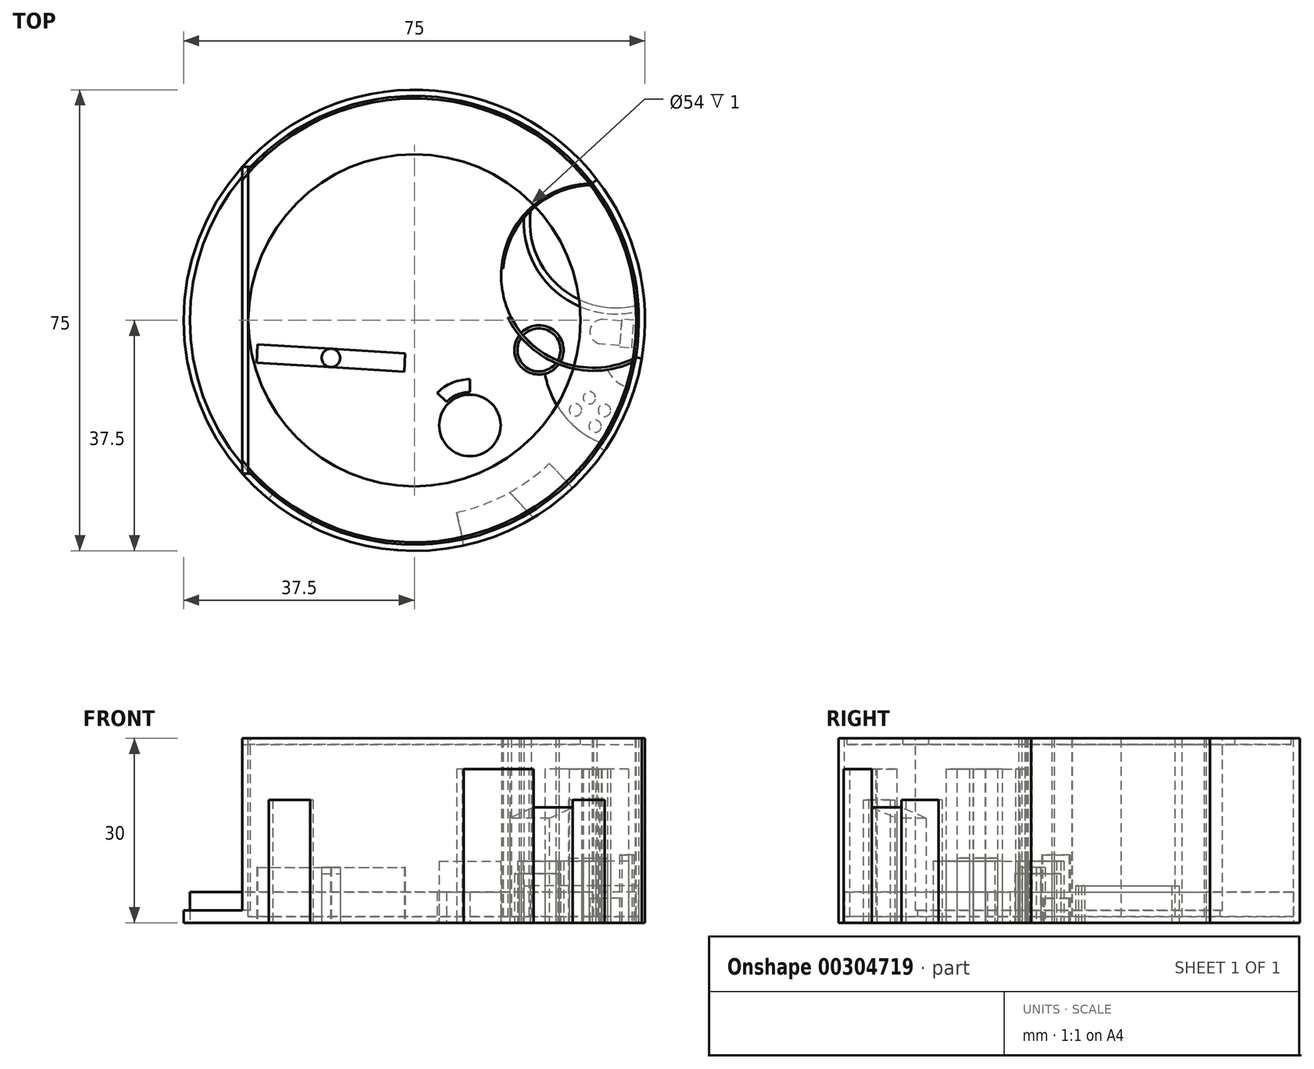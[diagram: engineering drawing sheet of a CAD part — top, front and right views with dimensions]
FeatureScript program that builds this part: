
annotation { "Feature Type Name" : "Feature", "Feature Type Description" : "" }
export const myFeature = defineFeature(function(context is Context, id is Id, definition is map)
    precondition{}
    {
        {
            var Q0;
            Q0=qCreatedBy(makeId("Top.planeOp"),FACE);
            var sketch = newSketch(context, id + "F0", { "sketchPlane" : qUnion([Q0])});
            skCircle(sketch, "E0", {"center": v(0, 0) * mm, "radius": 37.5 * mm});
            skSolve(sketch);
        }
        {
            var Q0;
            Q0=makeQuery(id+"F0.imprint","IMPRINT",FACE,{"disambiguationData":[TD([[makeQuery(id+"F0.imprint","IMPRINT",EDGE,{"derivedFrom":sQuery(id+"F0.wireOp",EDGE,"E0")}),1.0]])]});
            extrude(context, id + "F1", {"entities" : qUnion([Q0]), "oppositeDirection" : true, "depth" : 30 * mm});
        }
        {
            var Q0;
            Q0=qSketchRegion(id+"F0",true);
            var sketch = newSketch(context, id + "F2", { "sketchPlane" : qUnion([Q0])});
            skLineSegment(sketch, "E1", {"start": v(-28, 24.94) * mm, "end": v(-28, -24.94) * mm});
            skSolve(sketch);
        }
        {
            var Q0;
            {var subQ0=sQuery(id+"F2.wireOp",EDGE,"E1");Q0=makeQuery(id+"F2.imprint","IMPRINT",FACE,{"disambiguationData":[TD([[makeQuery(id+"F2.imprint","IMPRINT",EDGE,{"derivedFrom":subQ0}),-1.0]])]});}
            extrude(context, id + "F3", {"entities" : qUnion([Q0]), "operationType" : NewBodyOperationType.REMOVE, "oppositeDirection" : true, "depth" : 28 * mm});
        }
        {
            var Q0;
            {var subQ0=sQuery(id+"F2.wireOp",EDGE,"E1");Q0=makeQuery(id+"F2.imprint","IMPRINT",FACE,{"disambiguationData":[TD([[makeQuery(id+"F2.imprint","IMPRINT",EDGE,{"derivedFrom":subQ0}),1.0]])]});}
            var sketch = newSketch(context, id + "F4", { "sketchPlane" : qUnion([Q0])});
            skCircle(sketch, "E2", {"center": v(0, 0) * mm, "radius": 27 * mm});
            skArc(sketch, "E3", {"start": v(-28, 22.79) * mm, "mid": v(36.1, 0) * mm, "end": v(-28, -22.79) * mm});
            skLineSegment(sketch, "E4", {"start": v(-28, -22.79) * mm, "end": v(-28, 22.79) * mm});
            skSolve(sketch);
        }
        {
            var Q0;
            {var subQ0=sQuery(id+"F2.wireOp",EDGE,"E1");Q0=makeQuery(id+"F2.imprint","IMPRINT",FACE,{"disambiguationData":[TD([[makeQuery(id+"F2.imprint","IMPRINT",EDGE,{"derivedFrom":subQ0}),1.0]])]});}
            var sketch = newSketch(context, id + "F5", { "sketchPlane" : qUnion([Q0])});
            skArc(sketch, "E5", {"start": v(-23.66, -29.1) * mm, "mid": v(-20.43, -31.45) * mm, "end": v(-16.95, -33.45) * mm});
            skSolve(sketch);
        }
        {
            var Q0;
            Q0=makeQuery(id+"F1.opExtrude","CAP_FACE",FACE,{"disambiguationData":[OSD([sQuery(id+"F0.wireOp",EDGE,"E0")])],"isStart":false});
            var sketch = newSketch(context, id + "F6", { "sketchPlane" : qUnion([Q0])});
            skArc(sketch, "E6", {"start": v(-23.66, 29.1) * mm, "mid": v(-20.43, 31.45) * mm, "end": v(-16.95, 33.45) * mm});
            skArc(sketch, "E7", {"start": v(-23.03, 28.32) * mm, "mid": v(-19.88, 30.61) * mm, "end": v(-16.5, 32.56) * mm});
            skLineSegment(sketch, "E8", {"start": v(-23.66, 29.1) * mm, "end": v(-23.03, 28.32) * mm});
            skLineSegment(sketch, "E9", {"start": v(-16.95, 33.45) * mm, "end": v(-16.5, 32.56) * mm});
            skLineSegment(sketch, "E10", {"start": v(0, 0) * mm, "end": v(-23.66, 29.1) * mm, "construction": true});
            skLineSegment(sketch, "E11", {"start": v(-16.95, 33.45) * mm, "end": v(0, 0) * mm, "construction": true});
            skSolve(sketch);
        }
        {
            var Q0;
            Q0=makeQuery(id+"F1.opExtrude","CAP_FACE",FACE,{"disambiguationData":[OSD([sQuery(id+"F0.wireOp",EDGE,"E0")])],"isStart":false});
            var sketch = newSketch(context, id + "F7", { "sketchPlane" : qUnion([Q0])});
            skArc(sketch, "E12", {"start": v(8.05, 36.63) * mm, "mid": v(17.52, 33.15) * mm, "end": v(25.73, 27.28) * mm});
            skArc(sketch, "E13", {"start": v(25.73, 27.28) * mm, "mid": v(28.5, 24.38) * mm, "end": v(30.93, 21.2) * mm});
            skArc(sketch, "E14", {"start": v(30.93, 21.2) * mm, "mid": v(34.78, 14.03) * mm, "end": v(36.98, 6.2) * mm});
            skArc(sketch, "E15", {"start": v(36.98, 6.2) * mm, "mid": v(36.38, -9.1) * mm, "end": v(29.7, -22.9) * mm});
            skLineSegment(sketch, "E16", {"start": v(0, 0) * mm, "end": v(29.7, -22.9) * mm, "construction": true});
            skLineSegment(sketch, "E17", {"start": v(36.98, 6.2) * mm, "end": v(0, 0) * mm, "construction": true});
            skLineSegment(sketch, "E18", {"start": v(30.93, 21.2) * mm, "end": v(0, 0) * mm, "construction": true});
            skLineSegment(sketch, "E19", {"start": v(25.73, 27.28) * mm, "end": v(0, 0) * mm, "construction": true});
            skLineSegment(sketch, "E20", {"start": v(0, 0) * mm, "end": v(8.05, 36.63) * mm, "construction": true});
            skArc(sketch, "E21", {"start": v(6.87, 31.25) * mm, "mid": v(14.95, 28.3) * mm, "end": v(21.96, 23.28) * mm});
            skArc(sketch, "E22", {"start": v(31.56, 5.3) * mm, "mid": v(29.67, 11.98) * mm, "end": v(26.4, 18.1) * mm});
            skLineSegment(sketch, "E23", {"start": v(25.73, 27.28) * mm, "end": v(21.96, 23.28) * mm});
            skLineSegment(sketch, "E24", {"start": v(8.05, 36.63) * mm, "end": v(6.87, 31.25) * mm});
            skLineSegment(sketch, "E25", {"start": v(26.4, 18.1) * mm, "end": v(30.93, 21.2) * mm});
            skLineSegment(sketch, "E26", {"start": v(31.56, 5.3) * mm, "end": v(36.98, 6.2) * mm});
            skArc(sketch, "E27", {"start": v(25.04, 26.55) * mm, "mid": v(27.73, 23.73) * mm, "end": v(30.1, 20.64) * mm});
            skLineSegment(sketch, "E28", {"start": v(30.93, 21.2) * mm, "end": v(30.1, 20.64) * mm});
            skLineSegment(sketch, "E29", {"start": v(25.73, 27.28) * mm, "end": v(25.04, 26.55) * mm});
            skArc(sketch, "E30", {"start": v(36, 6.04) * mm, "mid": v(35.4, -8.86) * mm, "end": v(28.9, -22.29) * mm});
            skLineSegment(sketch, "E31", {"start": v(29.7, -22.9) * mm, "end": v(28.9, -22.29) * mm});
            skLineSegment(sketch, "E32", {"start": v(19.37, 32.1) * mm, "end": v(15.5, 28) * mm});
            skSolve(sketch);
        }
        {
            var Q0;
            Q0=makeQuery(id+"F1.opExtrude","CAP_FACE",FACE,{"disambiguationData":[OSD([sQuery(id+"F0.wireOp",EDGE,"E0")])],"isStart":true});
            shell(context, id + "F8", {"entities" : qUnion([Q0]), "thickness" : 1 * mm});
        }
        {
            var Q0;
            Q0=qSketchRegion(id+"F6",true);
            extrude(context, id + "F9", {"entities" : qUnion([Q0]), "operationType" : NewBodyOperationType.REMOVE, "oppositeDirection" : true, "depth" : 20 * mm});
        }
        {
            var Q0;
            Q0=qSketchRegion(id+"F6",true);
            extrude(context, id + "F10", {"entities" : qUnion([Q0]), "oppositeDirection" : true, "depth" : 20 * mm});
        }
        {
            var Q0;
            Q0=makeQuery(id+"F7.imprint","IMPRINT",FACE,{"disambiguationData":[TD([[makeQuery(id+"F7.imprint","IMPRINT",EDGE,{"derivedFrom":sQuery(id+"F7.wireOp",EDGE,"E12")}),-1.0]])]});
            extrude(context, id + "F11", {"entities" : qUnion([Q0]), "operationType" : NewBodyOperationType.REMOVE, "oppositeDirection" : true, "depth" : 25 * mm});
        }
        {
            var Q0;
            Q0=makeQuery(id+"F7.imprint","IMPRINT",FACE,{"disambiguationData":[TD([[makeQuery(id+"F7.imprint","IMPRINT",EDGE,{"derivedFrom":sQuery(id+"F7.wireOp",EDGE,"E12")}),-1.0]])]});
            extrude(context, id + "F12", {"entities" : qUnion([Q0]), "oppositeDirection" : true, "depth" : 25 * mm});
        }
        {
            var Q0;
            {var subQ0=sQuery(id+"F7.wireOp",EDGE,"E15");Q0=makeQuery(id+"F7.imprint","IMPRINT",FACE,{"disambiguationData":[TD([[makeQuery(id+"F7.imprint","IMPRINT",EDGE,{"derivedFrom":subQ0}),-1.0]])]});}
            extrude(context, id + "F13", {"entities" : qUnion([Q0]), "operationType" : NewBodyOperationType.REMOVE, "oppositeDirection" : true, "depth" : 30 * mm});
        }
        {
            var Q0;
            {var subQ0=sQuery(id+"F7.wireOp",EDGE,"E15");Q0=makeQuery(id+"F7.imprint","IMPRINT",FACE,{"disambiguationData":[TD([[makeQuery(id+"F7.imprint","IMPRINT",EDGE,{"derivedFrom":subQ0}),-1.0]])]});}
            extrude(context, id + "F14", {"entities" : qUnion([Q0]), "oppositeDirection" : true, "depth" : 30 * mm});
        }
        {
            var Q0;
            Q0=makeQuery(id+"F7.imprint","IMPRINT",FACE,{"disambiguationData":[TD([[makeQuery(id+"F7.imprint","IMPRINT",EDGE,{"derivedFrom":sQuery(id+"F7.wireOp",EDGE,"E13")}),-1.0]])]});
            extrude(context, id + "F15", {"entities" : qUnion([Q0]), "operationType" : NewBodyOperationType.REMOVE, "oppositeDirection" : true, "depth" : 20 * mm});
        }
        {
            var Q0;
            Q0=makeQuery(id+"F7.imprint","IMPRINT",FACE,{"disambiguationData":[TD([[makeQuery(id+"F7.imprint","IMPRINT",EDGE,{"derivedFrom":sQuery(id+"F7.wireOp",EDGE,"E13")}),-1.0]])]});
            extrude(context, id + "F16", {"entities" : qUnion([Q0]), "oppositeDirection" : true, "depth" : 20 * mm});
        }
        {
            var Q0;
            Q0=makeQuery(id+"F3.boolean.opBoolean","COPY",FACE,{"derivedFrom":makeQuery(id+"F3.opExtrude","SWEPT_FACE",FACE,{"disambiguationData":[OSD([sQuery(id+"F2.wireOp",EDGE,"E1")])]})});
            var sketch = newSketch(context, id + "F17", { "sketchPlane" : qUnion([Q0])});
            skLineSegment(sketch, "E33", {"start": v(24.94, -28) * mm, "end": v(24.94, 0) * mm});
            skLineSegment(sketch, "E34", {"start": v(24.94, 0) * mm, "end": v(-24.94, 0) * mm});
            skLineSegment(sketch, "E35", {"start": v(-24.94, 0) * mm, "end": v(-24.94, -28) * mm});
            skLineSegment(sketch, "E36", {"start": v(-24.94, -28) * mm, "end": v(24.94, -28) * mm});
            skSolve(sketch);
        }
        {
            var Q0;
            Q0=makeQuery(id+"F17.imprint","IMPRINT",FACE,{"disambiguationData":[TD([[makeQuery(id+"F17.imprint","IMPRINT",EDGE,{"derivedFrom":sQuery(id+"F17.wireOp",EDGE,"E33")}),1.0]])]});
            extrude(context, id + "F18", {"entities" : qUnion([Q0]), "operationType" : NewBodyOperationType.REMOVE, "endBound" : BoundingType.UP_TO_NEXT, "oppositeDirection" : true, "depth" : 25 * mm});
        }
        {
            var Q0;
            Q0=makeQuery(id+"F17.imprint","IMPRINT",FACE,{"disambiguationData":[TD([[makeQuery(id+"F17.imprint","IMPRINT",EDGE,{"derivedFrom":sQuery(id+"F17.wireOp",EDGE,"E33")}),1.0]])]});
            extrude(context, id + "F19", {"entities" : qUnion([Q0]), "oppositeDirection" : true, "depth" : 1 * mm});
        }
        {
            var Q0;
            Q0=makeQuery(id+"F6.imprint","IMPRINT",FACE,{"disambiguationData":[TD([[makeQuery(id+"F6.imprint","IMPRINT",EDGE,{"derivedFrom":sQuery(id+"F6.wireOp",EDGE,"E7")}),-1.0]])]});
            var sketch = newSketch(context, id + "F20", { "sketchPlane" : qUnion([Q0])});
            skCircle(sketch, "E37", {"center": v(-1.82, -23.91) * mm, "radius": 12.12 * mm});
            skCircle(sketch, "E38", {"center": v(-13.57, 6.12) * mm, "radius": 12.12 * mm});
            skArc(sketch, "E39", {"start": v(28.9, -22.29) * mm, "mid": v(35.4, -8.86) * mm, "end": v(36, 6.04) * mm});
            skArc(sketch, "E40", {"start": v(28.9, -22.29) * mm, "mid": v(14.56, -3.65) * mm, "end": v(36, 6.04) * mm});
            skArc(sketch, "E41", {"start": v(28.9, -22.29) * mm, "mid": v(-35.4, 8.86) * mm, "end": v(36, 6.04) * mm});
            skLineSegment(sketch, "E42", {"start": v(15.9, -14.39) * mm, "end": v(8.85, -18.17) * mm});
            skLineSegment(sketch, "E43", {"start": v(-6.24, -12.62) * mm, "end": v(-9.15, -5.17) * mm});
            skLineSegment(sketch, "E44", {"start": v(-13.57, 6.12) * mm, "end": v(-1.82, -23.91) * mm, "construction": true});
            skLineSegment(sketch, "E45", {"start": v(-1.82, -23.91) * mm, "end": v(29.11, -7.29) * mm, "construction": true});
            skLineSegment(sketch, "E46", {"start": v(-2.66, 11.41) * mm, "end": v(4.53, 14.9) * mm});
            skLineSegment(sketch, "E47", {"start": v(-13.57, 6.12) * mm, "end": v(9.03, 17.09) * mm, "construction": true});
            skPoint(sketch, "E48.middle", {"position": v(9.03, 17.09) * mm});
            skArc(sketch, "E49", {"start": v(9.03, 11.68) * mm, "mid": v(6.96, 12.1) * mm, "end": v(5.2, 13.26) * mm});
            skArc(sketch, "E50", {"start": v(3.73, 11.79) * mm, "mid": v(6.16, 10.16) * mm, "end": v(9.03, 9.59) * mm});
            skArc(sketch, "E51", {"start": v(14.33, 11.79) * mm, "mid": v(15.96, 14.22) * mm, "end": v(16.53, 17.09) * mm});
            skArc(sketch, "E52", {"start": v(14.44, 17.09) * mm, "mid": v(14.03, 15.02) * mm, "end": v(12.86, 13.26) * mm});
            skArc(sketch, "E53", {"start": v(12.86, 20.91) * mm, "mid": v(11.1, 22.09) * mm, "end": v(9.03, 22.5) * mm});
            skArc(sketch, "E54", {"start": v(14.33, 22.4) * mm, "mid": v(11.9, 24.02) * mm, "end": v(9.03, 24.59) * mm});
            skArc(sketch, "E55", {"start": v(5.2, 20.91) * mm, "mid": v(4.03, 19.16) * mm, "end": v(3.62, 17.09) * mm});
            skArc(sketch, "E56", {"start": v(3.73, 22.4) * mm, "mid": v(2.1, 19.96) * mm, "end": v(1.53, 17.09) * mm});
            skLineSegment(sketch, "E57", {"start": v(16.53, 17.09) * mm, "end": v(14.44, 17.09) * mm});
            skLineSegment(sketch, "E58", {"start": v(12.86, 13.26) * mm, "end": v(14.33, 11.79) * mm});
            skLineSegment(sketch, "E59", {"start": v(9.03, 11.68) * mm, "end": v(9.03, 9.59) * mm});
            skLineSegment(sketch, "E60", {"start": v(5.2, 13.26) * mm, "end": v(3.73, 11.79) * mm});
            skLineSegment(sketch, "E61", {"start": v(3.62, 17.09) * mm, "end": v(1.53, 17.09) * mm});
            skLineSegment(sketch, "E62", {"start": v(5.2, 20.91) * mm, "end": v(3.73, 22.4) * mm});
            skLineSegment(sketch, "E63", {"start": v(9.03, 22.5) * mm, "end": v(9.03, 24.59) * mm});
            skLineSegment(sketch, "E64", {"start": v(12.86, 20.91) * mm, "end": v(14.33, 22.4) * mm});
            skCircle(sketch, "E65", {"center": v(9.03, 17.09) * mm, "radius": 5 * mm});
            skLineSegment(sketch, "E66", {"start": v(9.03, 17.09) * mm, "end": v(6.87, 31.25) * mm, "construction": true});
            skLineSegment(sketch, "E67", {"start": v(9.03, 17.09) * mm, "end": v(21.96, 23.28) * mm, "construction": true});
            skSolve(sketch);
        }
        {
            var Q0;
            Q0=makeQuery(id+"F6.imprint","IMPRINT",FACE,{"disambiguationData":[TD([[makeQuery(id+"F6.imprint","IMPRINT",EDGE,{"derivedFrom":sQuery(id+"F6.wireOp",EDGE,"E7")}),-1.0]])]});
            var sketch = newSketch(context, id + "F21", { "sketchPlane" : qUnion([Q0])});
            skCircle(sketch, "E68", {"center": v(-13.57, 6.12) * mm, "radius": 1.5 * mm});
            skLineSegment(sketch, "E69", {"start": v(-25.66, 6.88) * mm, "end": v(-1.65, 8.34) * mm});
            skLineSegment(sketch, "E70", {"start": v(-25.48, 3.89) * mm, "end": v(-1.47, 5.35) * mm});
            skArc(sketch, "E71", {"start": v(30.53, 20) * mm, "mid": v(24.4, 15.56) * mm, "end": v(21.23, 8.7) * mm});
            skLineSegment(sketch, "E72", {"start": v(35.36, 4.48) * mm, "end": v(35.7, 0) * mm});
            skLineSegment(sketch, "E73", {"start": v(35.7, 0) * mm, "end": v(33.71, -0.16) * mm});
            skLineSegment(sketch, "E74", {"start": v(33.71, -0.16) * mm, "end": v(33.37, 4.33) * mm});
            skLineSegment(sketch, "E75", {"start": v(33.37, 4.33) * mm, "end": v(35.36, 4.48) * mm});
            skLineSegment(sketch, "E76", {"start": v(33.7, 0.1) * mm, "end": v(30.7, -0.14) * mm});
            skLineSegment(sketch, "E77", {"start": v(33.38, 4.08) * mm, "end": v(30.4, 3.85) * mm});
            skArc(sketch, "E78", {"start": v(30.4, 3.85) * mm, "mid": v(28.55, 1.7) * mm, "end": v(30.7, -0.14) * mm});
            skArc(sketch, "E79", {"start": v(17.83, -17.17) * mm, "mid": v(23.13, -4.56) * mm, "end": v(36.47, -1.5) * mm});
            skArc(sketch, "E80", {"start": v(36, 6.04) * mm, "mid": v(14.56, -3.65) * mm, "end": v(28.9, -22.29) * mm, "construction": true});
            skArc(sketch, "E81", {"start": v(28.52, -22.78) * mm, "mid": v(14.08, -3.52) * mm, "end": v(35.89, 6.65) * mm, "construction": true});
            skArc(sketch, "E82", {"start": v(36, 6.04) * mm, "mid": v(24.55, 7) * mm, "end": v(15.77, -0.43) * mm});
            skArc(sketch, "E83", {"start": v(35.89, 6.65) * mm, "mid": v(24.07, 7.37) * mm, "end": v(15.2, -0.47) * mm});
            skArc(sketch, "E84", {"start": v(28.9, -22.29) * mm, "mid": v(18.85, -18.23) * mm, "end": v(14.16, -8.45) * mm});
            skArc(sketch, "E85", {"start": v(28.52, -22.78) * mm, "mid": v(18.37, -18.46) * mm, "end": v(13.66, -8.49) * mm});
            skLineSegment(sketch, "E86", {"start": v(15.2, -0.47) * mm, "end": v(15.77, -0.43) * mm});
            skArc(sketch, "E87", {"start": v(14.46, -8.43) * mm, "mid": v(19.13, -18.08) * mm, "end": v(29.11, -21.99) * mm});
            skArc(sketch, "E88", {"start": v(28.29, -23.07) * mm, "mid": v(18.08, -18.6) * mm, "end": v(13.36, -8.51) * mm});
            skLineSegment(sketch, "E89", {"start": v(13.36, -8.51) * mm, "end": v(13.66, -8.49) * mm});
            skLineSegment(sketch, "E90", {"start": v(14.16, -8.45) * mm, "end": v(14.46, -8.43) * mm});
            skLineSegment(sketch, "E91", {"start": v(28.9, -22.29) * mm, "end": v(29.11, -21.99) * mm});
            skLineSegment(sketch, "E92", {"start": v(28.29, -23.07) * mm, "end": v(28.52, -22.78) * mm});
            skCircle(sketch, "E93", {"center": v(26.2, 14.57) * mm, "radius": 1 * mm});
            skCircle(sketch, "E94", {"center": v(29.39, 17.23) * mm, "radius": 1 * mm});
            skCircle(sketch, "E95", {"center": v(30.91, 14.65) * mm, "radius": 1 * mm});
            skCircle(sketch, "E96", {"center": v(28.45, 12.6) * mm, "radius": 1 * mm});
            skLineSegment(sketch, "E97", {"start": v(-1.47, 5.35) * mm, "end": v(-1.65, 8.34) * mm});
            skLineSegment(sketch, "E98", {"start": v(-25.48, 3.89) * mm, "end": v(-25.66, 6.88) * mm});
            skArc(sketch, "E99", {"start": v(17.7, 2.43) * mm, "mid": v(22.32, 2) * mm, "end": v(23.3, 6.54) * mm});
            skArc(sketch, "E100", {"start": v(23.77, 6.73) * mm, "mid": v(22.62, 1.59) * mm, "end": v(17.37, 2.04) * mm});
            skArc(sketch, "E101", {"start": v(17.37, 2.83) * mm, "mid": v(18.19, 7.64) * mm, "end": v(23.02, 6.96) * mm});
            skArc(sketch, "E102", {"start": v(17.04, 2.43) * mm, "mid": v(17.9, 8.04) * mm, "end": v(23.5, 7.16) * mm});
            skLineSegment(sketch, "E103", {"start": v(17.04, 2.43) * mm, "end": v(17.37, 2.83) * mm});
            skLineSegment(sketch, "E104", {"start": v(17.37, 2.04) * mm, "end": v(17.7, 2.43) * mm});
            skLineSegment(sketch, "E105", {"start": v(23.3, 6.54) * mm, "end": v(23.77, 6.73) * mm});
            skLineSegment(sketch, "E106", {"start": v(23.02, 6.96) * mm, "end": v(23.5, 7.16) * mm});
            skLineSegment(sketch, "E107", {"start": v(36, 6.04) * mm, "end": v(35.89, 6.65) * mm});
            skArc(sketch, "E108", {"start": v(30.53, 20) * mm, "mid": v(33.87, 13.6) * mm, "end": v(35.89, 6.65) * mm});
            skArc(sketch, "E109", {"start": v(36.41, -2.52) * mm, "mid": v(23.38, -5.68) * mm, "end": v(18.98, -18.34) * mm});
            skLineSegment(sketch, "E110", {"start": v(36.47, -1.5) * mm, "end": v(36.41, -2.52) * mm});
            skLineSegment(sketch, "E111", {"start": v(17.83, -17.17) * mm, "end": v(18.98, -18.34) * mm});
            skLineSegment(sketch, "E112", {"start": v(36, 6.04) * mm, "end": v(20.25, 4.82) * mm, "construction": true});
            skLineSegment(sketch, "E113", {"start": v(36, 6.04) * mm, "end": v(24.68, 15.88) * mm, "construction": true});
            skLineSegment(sketch, "E114", {"start": v(36, 6.04) * mm, "end": v(28.37, 18.95) * mm, "construction": true});
            skArc(sketch, "E115", {"start": v(31.6, 18.27) * mm, "mid": v(25.84, 14.15) * mm, "end": v(23.1, 7.63) * mm, "construction": true});
            skArc(sketch, "E116", {"start": v(33, 15.58) * mm, "mid": v(28.54, 12.7) * mm, "end": v(26.18, 7.93) * mm, "construction": true});
            skArc(sketch, "E117", {"start": v(31.41, 8.04) * mm, "mid": v(32.79, 9.87) * mm, "end": v(34.83, 10.9) * mm});
            skSolve(sketch);
        }
        {
            var Q0;
            {var subQ0=sQuery(id+"F20.wireOp",EDGE,"E38");var subQ1=makeQuery(id+"F20.imprint","IMPRINT",VERTEX,{"disambiguationData":[OD(0.0)],"derivedFrom":subQ0});Q0=makeQuery(id+"F20.imprint","IMPRINT",FACE,{"disambiguationData":[TD([[makeQuery(id+"F20.imprint","IMPRINT",EDGE,{"disambiguationData":[TD([[subQ1,1.0]])],"derivedFrom":subQ0}),1.0]])]});}
            var Q1;
            {var subQ0=sQuery(id+"F20.wireOp",EDGE,"E37");var subQ1=makeQuery(id+"F20.imprint","IMPRINT",VERTEX,{"disambiguationData":[OD(0.0)],"derivedFrom":subQ0});Q1=makeQuery(id+"F20.imprint","IMPRINT",FACE,{"disambiguationData":[TD([[makeQuery(id+"F20.imprint","IMPRINT",EDGE,{"disambiguationData":[TD([[subQ1,-1.0]])],"derivedFrom":subQ0}),1.0]])]});}
            var Q2;
            Q2=makeQuery(id+"F20.imprint","IMPRINT",FACE,{"disambiguationData":[TD([[makeQuery(id+"F20.imprint","IMPRINT",EDGE,{"derivedFrom":sQuery(id+"F20.wireOp",EDGE,"E55")}),-1.0]])]});
            var Q3;
            Q3=makeQuery(id+"F20.imprint","IMPRINT",FACE,{"disambiguationData":[TD([[makeQuery(id+"F20.imprint","IMPRINT",EDGE,{"derivedFrom":sQuery(id+"F20.wireOp",EDGE,"E49")}),1.0]])]});
            var Q4;
            Q4=makeQuery(id+"F20.imprint","IMPRINT",FACE,{"disambiguationData":[TD([[makeQuery(id+"F20.imprint","IMPRINT",EDGE,{"derivedFrom":sQuery(id+"F20.wireOp",EDGE,"E51")}),1.0]])]});
            var Q5;
            Q5=makeQuery(id+"F20.imprint","IMPRINT",FACE,{"disambiguationData":[TD([[makeQuery(id+"F20.imprint","IMPRINT",EDGE,{"derivedFrom":sQuery(id+"F20.wireOp",EDGE,"E53")}),-1.0]])]});
            extrude(context, id + "F22", {"entities" : qUnion([Q0, Q1, Q2, Q3, Q4, Q5]), "oppositeDirection" : true, "depth" : 5 * mm});
        }
        {
            var Q0;
            Q0=makeQuery(id+"F20.imprint","IMPRINT",FACE,{"disambiguationData":[TD([[makeQuery(id+"F20.imprint","IMPRINT",EDGE,{"derivedFrom":sQuery(id+"F20.wireOp",EDGE,"E65")}),1.0]])]});
            extrude(context, id + "F23", {"entities" : qUnion([Q0]), "oppositeDirection" : true, "depth" : 10 * mm});
        }
        {
            var Q0;
            {var subQ5=sQuery(id+"F21.wireOp",EDGE,"E97");Q0=makeQuery(id+"F21.imprint","IMPRINT",FACE,{"disambiguationData":[TD([[makeQuery(id+"F21.imprint","IMPRINT",EDGE,{"derivedFrom":subQ5}),1.0]])]});}
            var Q1;
            {var subQ5=sQuery(id+"F21.wireOp",EDGE,"E98");Q1=makeQuery(id+"F21.imprint","IMPRINT",FACE,{"disambiguationData":[TD([[makeQuery(id+"F21.imprint","IMPRINT",EDGE,{"derivedFrom":subQ5}),-1.0]])]});}
            extrude(context, id + "F24", {"entities" : qUnion([Q0, Q1]), "oppositeDirection" : true, "depth" : 9 * mm});
        }
        {
            var Q0;
            {var subQ0=sQuery(id+"F21.wireOp",EDGE,"E68");var subQ1=makeQuery(id+"F21.imprint","INTERSECT",VERTEX,{"derivedFrom":[subQ0,sQuery(id+"F21.wireOp",EDGE,"E69")]});Q0=makeQuery(id+"F21.imprint","IMPRINT",FACE,{"disambiguationData":[TD([[makeQuery(id+"F21.imprint","IMPRINT",EDGE,{"disambiguationData":[TD([[subQ1,-1.0]])],"derivedFrom":subQ0}),1.0]])]});}
            extrude(context, id + "F25", {"entities" : qUnion([Q0]), "oppositeDirection" : true, "depth" : 8 * mm});
        }
        {
            var Q0;
            {var subQ0=sQuery(id+"F21.wireOp",EDGE,"E86");Q0=makeQuery(id+"F21.imprint","IMPRINT",FACE,{"disambiguationData":[TD([[makeQuery(id+"F21.imprint","IMPRINT",EDGE,{"derivedFrom":subQ0}),1.0]])]});}
            var Q1;
            {var subQ0=sQuery(id+"F21.wireOp",EDGE,"E91");Q1=makeQuery(id+"F21.imprint","IMPRINT",FACE,{"disambiguationData":[TD([[makeQuery(id+"F21.imprint","IMPRINT",EDGE,{"derivedFrom":subQ0}),1.0]])]});}
            var Q2;
            Q2=makeQuery(id+"F21.imprint","IMPRINT",FACE,{"disambiguationData":[TD([[makeQuery(id+"F21.imprint","IMPRINT",EDGE,{"derivedFrom":sQuery(id+"F21.wireOp",EDGE,"E85")}),1.0]])]});
            var Q3;
            {var subQ5=sQuery(id+"F21.wireOp",EDGE,"E90");Q3=makeQuery(id+"F21.imprint","IMPRINT",FACE,{"disambiguationData":[TD([[makeQuery(id+"F21.imprint","IMPRINT",EDGE,{"derivedFrom":subQ5}),-1.0]])]});}
            var Q4;
            {var subQ0=sQuery(id+"F21.wireOp",EDGE,"E111");Q4=makeQuery(id+"F21.imprint","IMPRINT",FACE,{"disambiguationData":[TD([[makeQuery(id+"F21.imprint","IMPRINT",EDGE,{"derivedFrom":subQ0}),1.0]])]});}
            extrude(context, id + "F26", {"entities" : qUnion([Q0, Q1, Q2, Q3, Q4]), "oppositeDirection" : true, "depth" : 30 * mm});
        }
        {
            var Q0;
            {var subQ0=sQuery(id+"F21.wireOp",EDGE,"E110");Q0=makeQuery(id+"F21.imprint","IMPRINT",FACE,{"disambiguationData":[TD([[makeQuery(id+"F21.imprint","IMPRINT",EDGE,{"derivedFrom":subQ0}),-1.0]])]});}
            extrude(context, id + "F27", {"entities" : qUnion([Q0]), "oppositeDirection" : true, "depth" : 6 * mm});
        }
        {
            var Q0;
            {var subQ0=sQuery(id+"F21.wireOp",EDGE,"E76");Q0=makeQuery(id+"F21.imprint","IMPRINT",FACE,{"disambiguationData":[TD([[makeQuery(id+"F21.imprint","IMPRINT",EDGE,{"derivedFrom":subQ0}),-1.0]])]});}
            extrude(context, id + "F28", {"entities" : qUnion([Q0]), "oppositeDirection" : true, "depth" : 4 * mm});
        }
        {
            var Q0;
            Q0=makeQuery(id+"F21.imprint","IMPRINT",FACE,{"disambiguationData":[TD([[makeQuery(id+"F21.imprint","IMPRINT",EDGE,{"derivedFrom":sQuery(id+"F21.wireOp",EDGE,"E96")}),1.0]])]});
            var Q1;
            Q1=makeQuery(id+"F21.imprint","IMPRINT",FACE,{"disambiguationData":[TD([[makeQuery(id+"F21.imprint","IMPRINT",EDGE,{"derivedFrom":sQuery(id+"F21.wireOp",EDGE,"E94")}),1.0]])]});
            var Q2;
            Q2=makeQuery(id+"F21.imprint","IMPRINT",FACE,{"disambiguationData":[TD([[makeQuery(id+"F21.imprint","IMPRINT",EDGE,{"derivedFrom":sQuery(id+"F21.wireOp",EDGE,"E93")}),1.0]])]});
            var Q3;
            Q3=makeQuery(id+"F21.imprint","IMPRINT",FACE,{"disambiguationData":[TD([[makeQuery(id+"F21.imprint","IMPRINT",EDGE,{"derivedFrom":sQuery(id+"F21.wireOp",EDGE,"E95")}),1.0]])]});
            extrude(context, id + "F29", {"entities" : qUnion([Q0, Q1, Q2, Q3]), "oppositeDirection" : true, "depth" : 10.5 * mm});
        }
        {
            var Q0;
            Q0=makeQuery(id+"F21.imprint","IMPRINT",FACE,{"disambiguationData":[TD([[makeQuery(id+"F21.imprint","IMPRINT",EDGE,{"derivedFrom":sQuery(id+"F21.wireOp",EDGE,"E72")}),-1.0]])]});
            extrude(context, id + "F30", {"entities" : qUnion([Q0]), "oppositeDirection" : true, "depth" : 11 * mm});
        }
        {
            var Q0;
            {var subQ5=sQuery(id+"F21.wireOp",EDGE,"E101");Q0=makeQuery(id+"F21.imprint","IMPRINT",FACE,{"disambiguationData":[TD([[makeQuery(id+"F21.imprint","IMPRINT",EDGE,{"derivedFrom":subQ5}),1.0]])]});}
            var Q1;
            Q1=makeQuery(id+"F21.imprint","IMPRINT",FACE,{"disambiguationData":[TD([[makeQuery(id+"F21.imprint","IMPRINT",EDGE,{"derivedFrom":sQuery(id+"F21.wireOp",EDGE,"E99")}),-1.0]])]});
            var Q2;
            {var subQ4=sQuery(id+"F21.wireOp",EDGE,"E71");Q2=makeQuery(id+"F21.imprint","IMPRINT",FACE,{"disambiguationData":[TD([[makeQuery(id+"F21.imprint","IMPRINT",EDGE,{"derivedFrom":subQ4}),1.0]])]});}
            extrude(context, id + "F31", {"entities" : qUnion([Q0, Q1, Q2]), "oppositeDirection" : true, "depth" : 10 * mm});
        }
        {
            var Q0;
            {var subQ0=sQuery(id+"F21.wireOp",EDGE,"E101");Q0=makeQuery(id+"F21.imprint","IMPRINT",FACE,{"disambiguationData":[TD([[makeQuery(id+"F21.imprint","IMPRINT",EDGE,{"derivedFrom":subQ0}),-1.0]])]});}
            var Q1;
            {var subQ0=sQuery(id+"F21.wireOp",EDGE,"E99");Q1=makeQuery(id+"F21.imprint","IMPRINT",FACE,{"disambiguationData":[TD([[makeQuery(id+"F21.imprint","IMPRINT",EDGE,{"derivedFrom":subQ0}),1.0]])]});}
            extrude(context, id + "F32", {"entities" : qUnion([Q0, Q1]), "oppositeDirection" : true, "depth" : 8 * mm});
        }
        {
            var Q0;
            {var subQ3=sQuery(id+"F21.wireOp",EDGE,"E117");Q0=makeQuery(id+"F21.imprint","IMPRINT",FACE,{"disambiguationData":[TD([[makeQuery(id+"F21.imprint","IMPRINT",EDGE,{"derivedFrom":subQ3}),-1.0]])]});}
            extrude(context, id + "F33", {"entities" : qUnion([Q0]), "oppositeDirection" : true, "depth" : 25 * mm});
        }
        {
            var Q0;
            {var subQ1=sQuery(id+"F7.wireOp",EDGE,"E23");Q0=makeQuery(id+"F7.imprint","IMPRINT",FACE,{"disambiguationData":[TD([[makeQuery(id+"F7.imprint","IMPRINT",EDGE,{"derivedFrom":subQ1}),-1.0]])]});}
            extrude(context, id + "F34", {"entities" : qUnion([Q0]), "oppositeDirection" : true, "depth" : 25 * mm});
        }
        {
            var Q0;
            Q0=makeQuery(id+"F34.opExtrude","CAP_EDGE",EDGE,{"disambiguationData":[OSD([sQuery(id+"F7.wireOp",EDGE,"E21")])],"isStart":false});
            chamfer(context, id + "F35", {"entities" : qUnion([Q0]), "chamferType" : ChamferType.TWO_OFFSETS, "width1" : 8 * mm, "oppositeDirection" : true, "width2" : 25 * mm, "tangentPropagation" : true});
        }
        {
            var Q0;
            Q0=makeQuery(id+"F4.imprint","IMPRINT",FACE,{"disambiguationData":[TD([[makeQuery(id+"F4.imprint","IMPRINT",EDGE,{"derivedFrom":sQuery(id+"F4.wireOp",EDGE,"E2")}),-1.0]])]});
            extrude(context, id + "F36", {"entities" : qUnion([Q0]), "oppositeDirection" : true, "depth" : 1 * mm});
        }
    });
